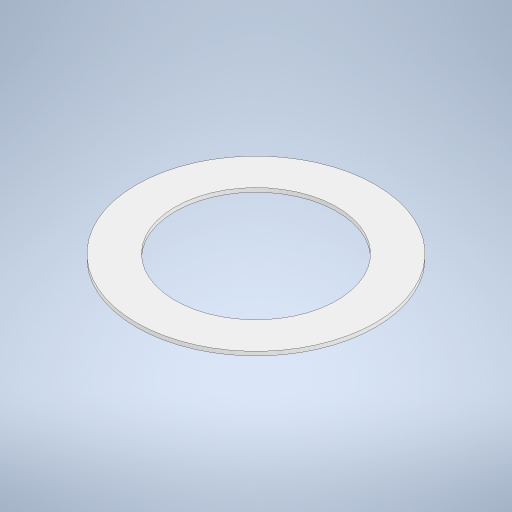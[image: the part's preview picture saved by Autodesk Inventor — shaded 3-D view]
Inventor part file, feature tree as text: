
AUTODESK INVENTOR PART (.ipt)
format: ipt  version: 2024.1 (Build 281209000, 209)  size: 228,352 bytes
history: native  units: in
note: dims shown in document units (in); Inventor stores cm internally (conversion verified against a paired STEP export)
features: extrude x1, sketch x1
ambient origin geometry x8: Origin, YZ Plane, XZ Plane, XY Plane, X Axis, Y Axis, Z Axis, Center Point
bodies: Solid1 (feature_tree)
feature tree (2):
  extrude  "Extrusion1"  Depth=0.0197in
  sketch  "Sketch1"  dims[d0=1.1811in d1=0.8in d2=0.0197in d3=0.0in]
